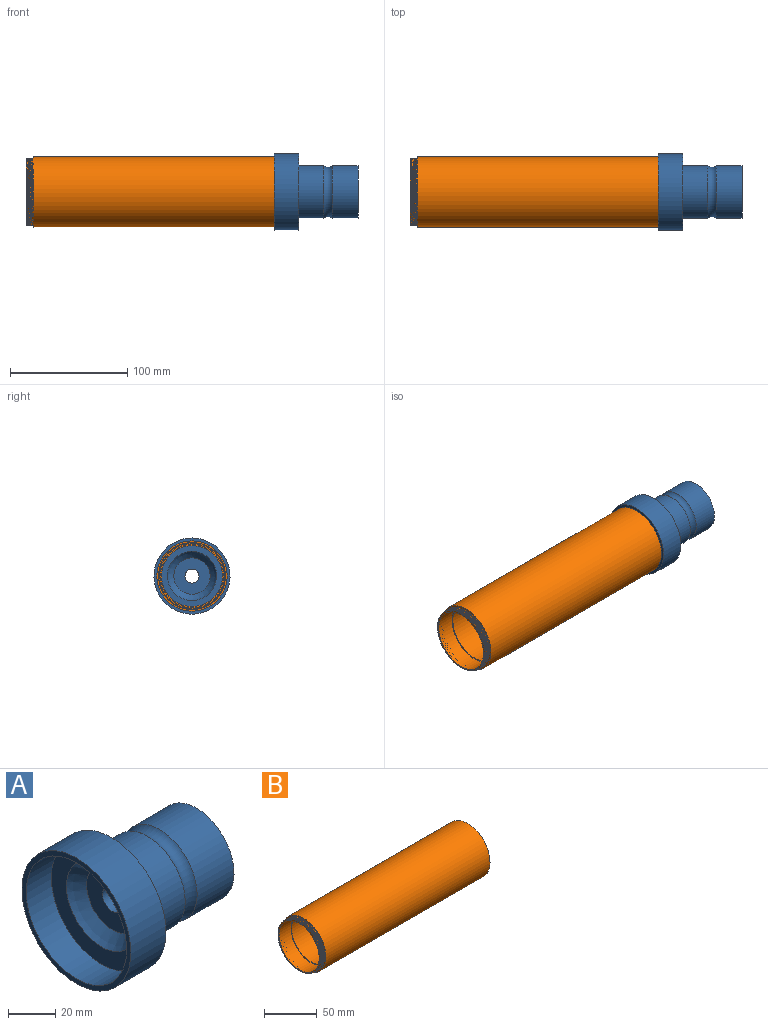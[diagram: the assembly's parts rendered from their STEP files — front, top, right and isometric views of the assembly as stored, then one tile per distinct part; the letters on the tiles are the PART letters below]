
ASSEMBLY  parts=2 mates=1
PART A: 14 faces, bbox 71.6x65x65 mm
  f0: cylinder r=15.5mm len=44mm, axis (-1,0,0), area 4285.1mm2, adj f1,f13
  f1: plane 45x45mm, normal (1,0,0), area 835.7mm2, adj f0,f2
  f2: cylinder r=22.5mm len=45mm, axis (-1,0,0), area 3114.3mm2, adj f1,f3
  f3: torus R=26mm, axis (-1,0,0), area 1075mm2, adj f2,f4
  f4: cylinder r=22.5mm len=45mm, axis (-1,0,0), area 3029.5mm2, adj f3,f5
  f5: plane 65x65mm, normal (1,0,0), area 1727.9mm2, adj f4,f6
  f6: cylinder r=32.5mm len=65mm, axis (-1,0,0), area 4288.3mm2, adj f5,f7
  f7: plane 65x65mm, normal (-1,0,0), area 490.9mm2, adj f6,f8
  f8: cylinder r=30mm len=60mm, axis (-1,0,0), area 2827.4mm2, adj f7,f9
  f9: plane 60x60mm, normal (-1,0,0), area 1442mm2, adj f8,f10
  f10: revolved ~42x42mm, area 1000.4mm2, adj f9,f11
  f11: plane 31x31mm, normal (-1,0,0), area 641.7mm2, adj f10,f12
  f12: cylinder r=6mm len=12mm, axis (-1,0,0), area 226.2mm2, adj f11,f13
  f13: plane 31x31mm, normal (1,0,0), area 641.7mm2, adj f0,f12
PART B: 13 faces, bbox 228x60.6x66.5 mm
  f0: cylinder r=30mm len=221mm, axis (-1,0,0), area 41657.5mm2, adj f4,f7
  f1: plane 57.64x57.39mm, normal (-1,0,0), area 236.9mm2, adj f5,f6,f8,f12
  f2: plane 54x54mm, normal (-1,0,0), area 166.5mm2, adj f3,f5
  f3: cylinder r=26mm len=211mm, axis (-1,0,0), area 34469.6mm2, adj f2,f4
  f4: plane 60x60mm, normal (1,0,0), area 703.7mm2, adj f0,f3
  f5: cylinder r=27mm len=54mm, axis (-1,0,0), area 2714.3mm2, adj f1,f2
  f6: cylinder r=28.5mm len=57mm, axis (-1,0,0), area 241.8mm2, adj f1,f7,f8,f9,f10,f12
  f7: plane 60x60mm, normal (-1,0,0), area 275.7mm2, adj f0,f6,f11
  f8: plane 0.69x0.4mm, normal (0,0,-1), area 0.1mm2, adj f1,f6,f10
  f9: plane 0.8x0.69mm, normal (0,0,1), area 0.3mm2, adj f6,f10,f11,f12
  f10: bspline ~65.82x57mm, area 848.9mm2, adj f6,f8,f9,f11,f12
  f11: cylinder r=28.5mm len=51.63mm, axis (1,0,0), area 14.4mm2, adj f7,f9,f10
  f12: bspline ~65.82x57mm, area 820.8mm2, adj f1,f6,f9,f10
PLACE A t=(-56.4,7.47,-48.9)mm
PLACE B t=(-56.4,7.47,-48.9)mm
MATE fastened A.f0 <-> B.f0  axis (-1,0,0) through (170.6,7.47,-48.9)mm
